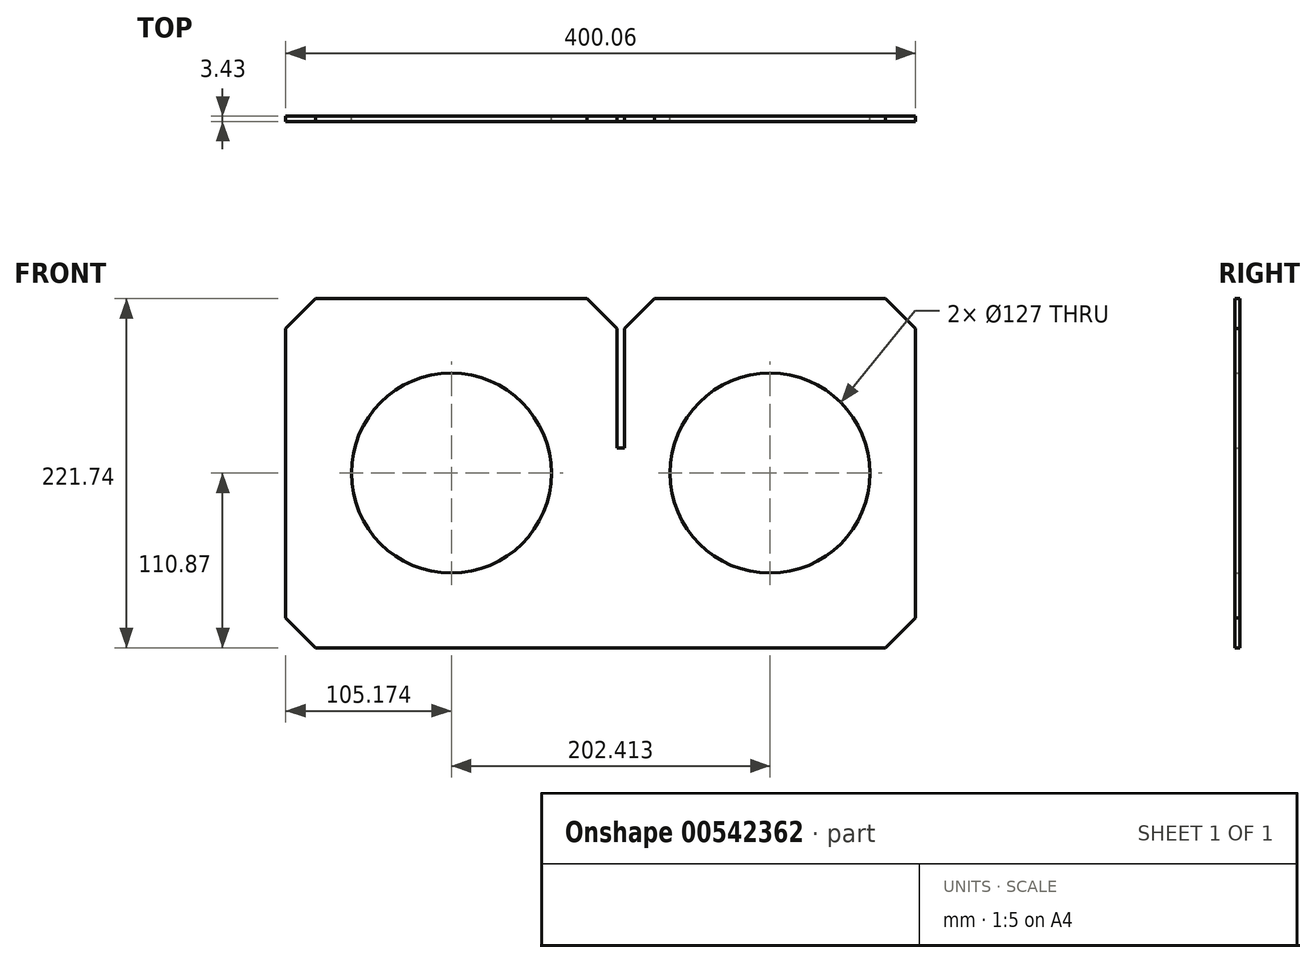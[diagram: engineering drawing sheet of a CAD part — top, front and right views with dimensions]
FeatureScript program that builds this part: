
annotation { "Feature Type Name" : "Feature", "Feature Type Description" : "" }
export const myFeature = defineFeature(function(context is Context, id is Id, definition is map)
    precondition{}
    {
        {
            var Q0;
            Q0=qCreatedBy(makeId("Front.planeOp"),FACE);
            var sketch = newSketch(context, id + "F0", { "sketchPlane" : qUnion([Q0])});
            skLineSegment(sketch, "E0.bottom", {"start": v(200.03, -110.87) * mm, "end": v(-200.03, -110.87) * mm});
            skLineSegment(sketch, "E0.left", {"start": v(200.03, -110.87) * mm, "end": v(200.03, 110.87) * mm});
            skLineSegment(sketch, "E0.right", {"start": v(-200.03, -110.87) * mm, "end": v(-200.03, 110.87) * mm});
            skPoint(sketch, "E0.middle", {"position": v(0, 0) * mm});
            skLineSegment(sketch, "E1.top", {"start": v(10.31, 16.13) * mm, "end": v(15.09, 16.13) * mm});
            skLineSegment(sketch, "E1.left", {"start": v(10.31, 110.87) * mm, "end": v(10.31, 16.13) * mm});
            skLineSegment(sketch, "E1.right", {"start": v(15.09, 110.87) * mm, "end": v(15.09, 16.13) * mm});
            skLineSegment(sketch, "E2", {"start": v(15.09, 110.87) * mm, "end": v(200.03, 110.87) * mm});
            skLineSegment(sketch, "E3", {"start": v(10.31, 110.87) * mm, "end": v(-200.03, 110.87) * mm});
            skPoint(sketch, "E4", {"position": v(-94.86, 110.87) * mm});
            skPoint(sketch, "E5", {"position": v(107.56, 110.87) * mm});
            skCircle(sketch, "E6", {"center": v(-94.86, 0) * mm, "radius": 63.5 * mm});
            skPoint(sketch, "E6.centerSnap0", {"position": v(-200.03, 0) * mm});
            skCircle(sketch, "E7", {"center": v(107.56, 0) * mm, "radius": 63.5 * mm});
            skPoint(sketch, "E7.centerSnap0", {"position": v(200.03, 0) * mm});
            skSolve(sketch);
        }
        {
            var Q0;
            Q0=makeQuery(id+"F0.imprint","IMPRINT",FACE,{"disambiguationData":[TD([[makeQuery(id+"F0.imprint","IMPRINT",EDGE,{"derivedFrom":sQuery(id+"F0.wireOp",EDGE,"E0.bottom")}),-1.0]])]});
            extrude(context, id + "F1", {"entities" : qUnion([Q0]), "depth" : 3.43 * mm, "offsetDistance" : 25.4 * mm});
        }
        {
            var Q0;
            Q0=makeQuery(id+"F1.opExtrude","SWEPT_EDGE",EDGE,{"disambiguationData":[OSD([sQuery(id+"F0.wireOp",EDGE,"E0.right"),sQuery(id+"F0.wireOp",EDGE,"E3")])]});
            var Q1;
            Q1=makeQuery(id+"F1.opExtrude","SWEPT_EDGE",EDGE,{"disambiguationData":[OSD([sQuery(id+"F0.wireOp",EDGE,"E1.left"),sQuery(id+"F0.wireOp",EDGE,"E3")])]});
            var Q2;
            Q2=makeQuery(id+"F1.opExtrude","SWEPT_EDGE",EDGE,{"disambiguationData":[OSD([sQuery(id+"F0.wireOp",EDGE,"E1.right"),sQuery(id+"F0.wireOp",EDGE,"E2")])]});
            var Q3;
            Q3=makeQuery(id+"F1.opExtrude","SWEPT_EDGE",EDGE,{"disambiguationData":[OSD([sQuery(id+"F0.wireOp",EDGE,"E0.left"),sQuery(id+"F0.wireOp",EDGE,"E2")])]});
            var Q4;
            Q4=makeQuery(id+"F1.opExtrude","SWEPT_EDGE",EDGE,{"disambiguationData":[OSD([sQuery(id+"F0.wireOp",EDGE,"E0.bottom"),sQuery(id+"F0.wireOp",EDGE,"E0.left")])]});
            var Q5;
            Q5=makeQuery(id+"F1.opExtrude","SWEPT_EDGE",EDGE,{"disambiguationData":[OSD([sQuery(id+"F0.wireOp",EDGE,"E0.bottom"),sQuery(id+"F0.wireOp",EDGE,"E0.right")])]});
            chamfer(context, id + "F2", {"entities" : qUnion([Q0, Q1, Q2, Q3, Q4, Q5]), "width" : 19.05 * mm, "tangentPropagation" : true});
        }
    });
